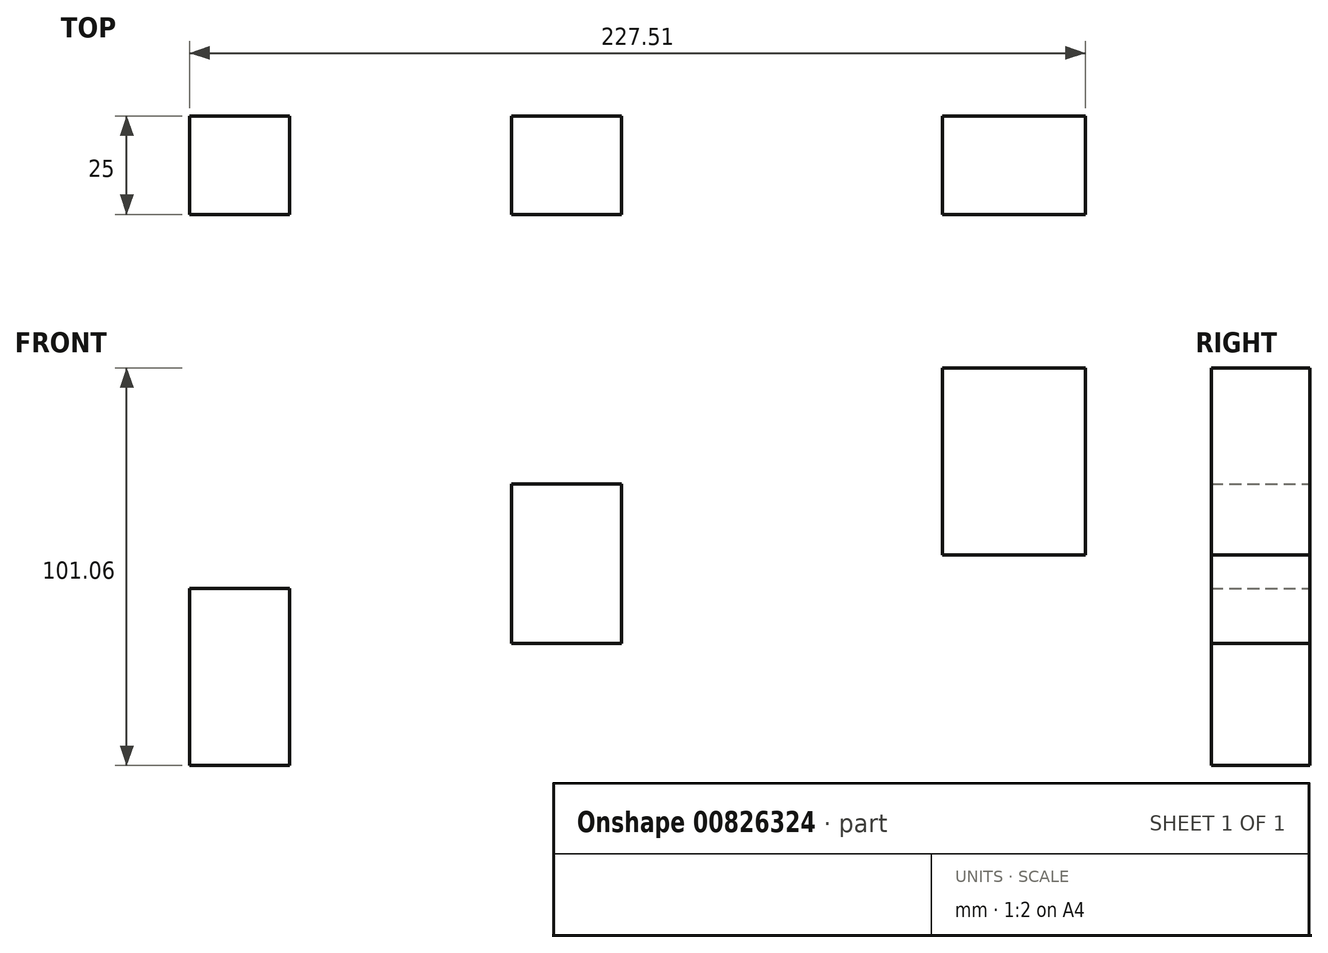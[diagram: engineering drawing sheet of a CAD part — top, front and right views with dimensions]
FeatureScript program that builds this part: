
annotation { "Feature Type Name" : "Feature", "Feature Type Description" : "" }
export const myFeature = defineFeature(function(context is Context, id is Id, definition is map)
    precondition{}
    {
        {
            var Q0;
            Q0=qCreatedBy(makeId("Front.planeOp"),FACE);
            var sketch = newSketch(context, id + "F0", { "sketchPlane" : qUnion([Q0])});
            skLineSegment(sketch, "E0.bottom", {"start": v(-105.64, 13.48) * mm, "end": v(-80.33, 13.48) * mm});
            skLineSegment(sketch, "E0.top", {"start": v(-105.64, 58.44) * mm, "end": v(-80.33, 58.44) * mm});
            skLineSegment(sketch, "E0.left", {"start": v(-105.64, 13.48) * mm, "end": v(-105.64, 58.44) * mm});
            skLineSegment(sketch, "E0.right", {"start": v(-80.33, 13.48) * mm, "end": v(-80.33, 58.44) * mm});
            skPoint(sketch, "E0.middle", {"position": v(-92.99, 35.96) * mm});
            skLineSegment(sketch, "E1.bottom", {"start": v(-23.86, 44.56) * mm, "end": v(4.06, 44.56) * mm});
            skLineSegment(sketch, "E1.top", {"start": v(-23.86, 85.07) * mm, "end": v(4.06, 85.07) * mm});
            skLineSegment(sketch, "E1.left", {"start": v(-23.86, 44.56) * mm, "end": v(-23.86, 85.07) * mm});
            skLineSegment(sketch, "E1.right", {"start": v(4.06, 44.56) * mm, "end": v(4.06, 85.07) * mm});
            skPoint(sketch, "E1.middle", {"position": v(-9.9, 64.81) * mm});
            skLineSegment(sketch, "E2.bottom", {"start": v(85.52, 67.04) * mm, "end": v(121.87, 67.04) * mm});
            skLineSegment(sketch, "E2.top", {"start": v(85.52, 114.54) * mm, "end": v(121.87, 114.54) * mm});
            skLineSegment(sketch, "E2.left", {"start": v(85.52, 67.04) * mm, "end": v(85.52, 114.54) * mm});
            skLineSegment(sketch, "E2.right", {"start": v(121.87, 67.04) * mm, "end": v(121.87, 114.54) * mm});
            skPoint(sketch, "E2.middle", {"position": v(103.7, 90.79) * mm});
            skSolve(sketch);
        }
        {
            var Q0;
            Q0 = qSketchRegion(id + "F0", true);
            extrude(context, id + "F1", {"entities" : qUnion([Q0]), "depth" : 25 * mm, "offsetDistance" : 25 * mm});
        }
    });
